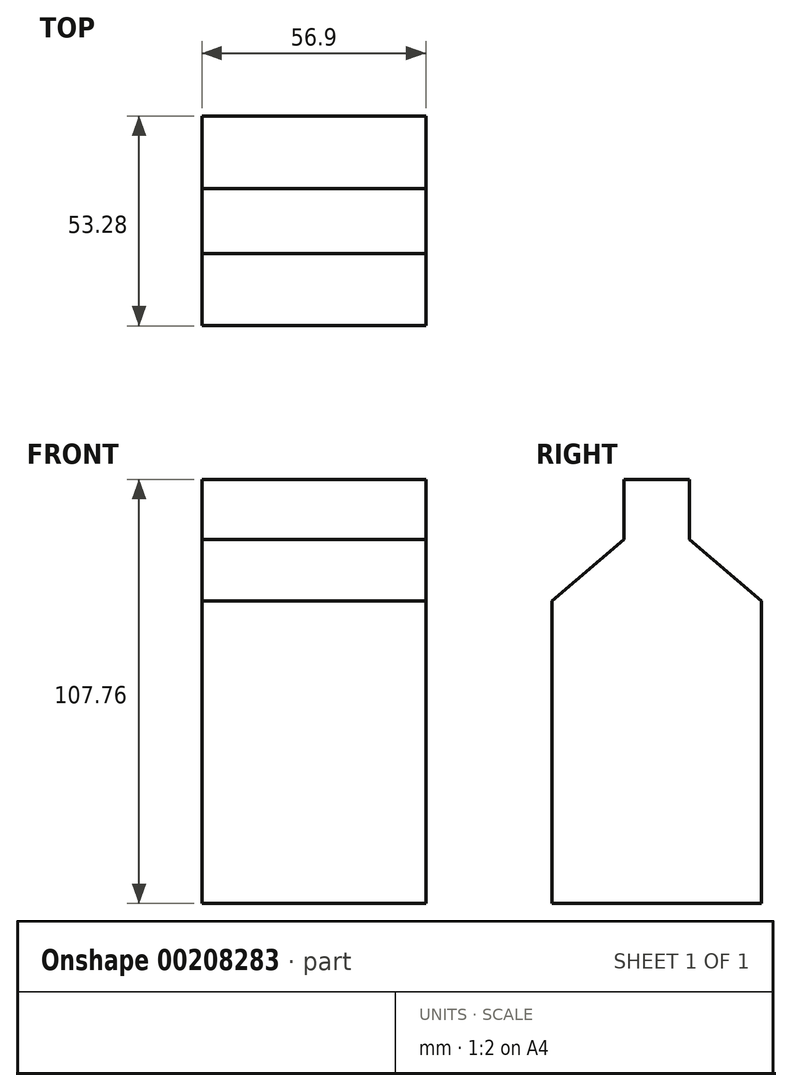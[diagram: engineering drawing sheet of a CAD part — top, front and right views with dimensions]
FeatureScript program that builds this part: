
annotation { "Feature Type Name" : "Feature", "Feature Type Description" : "" }
export const myFeature = defineFeature(function(context is Context, id is Id, definition is map)
    precondition{}
    {
        {
            var Q0;
            Q0=qCreatedBy(makeId("Right.planeOp"),FACE);
            var sketch = newSketch(context, id + "F0", { "sketchPlane" : qUnion([Q0])});
            skLineSegment(sketch, "E0.bottom", {"start": v(26.64, -38.44) * mm, "end": v(-26.64, -38.44) * mm});
            skLineSegment(sketch, "E0.left", {"start": v(26.64, -38.44) * mm, "end": v(26.64, 38.44) * mm});
            skLineSegment(sketch, "E0.right", {"start": v(-26.64, -38.44) * mm, "end": v(-26.64, 38.44) * mm});
            skPoint(sketch, "E0.middle", {"position": v(0, 0) * mm});
            skLineSegment(sketch, "E1", {"start": v(26.64, 38.44) * mm, "end": v(8.27, 53.98) * mm});
            skLineSegment(sketch, "E2", {"start": v(8.27, 53.98) * mm, "end": v(8.27, 69.32) * mm});
            skLineSegment(sketch, "E3", {"start": v(8.27, 69.32) * mm, "end": v(0, 69.32) * mm});
            skLineSegment(sketch, "E4.MirrorCS", {"start": v(-8.27, 69.32) * mm, "end": v(0, 69.32) * mm});
            skLineSegment(sketch, "E5.MirrorCS", {"start": v(-8.27, 53.98) * mm, "end": v(-8.27, 69.32) * mm});
            skLineSegment(sketch, "E6.MirrorCS", {"start": v(-26.64, 38.44) * mm, "end": v(-8.27, 53.98) * mm});
            skSolve(sketch);
        }
        {
            var Q0;
            Q0=makeQuery(id+"F0.imprint","IMPRINT",FACE,{"disambiguationData":[TD([[makeQuery(id+"F0.imprint","IMPRINT",EDGE,{"derivedFrom":sQuery(id+"F0.wireOp",EDGE,"E0.bottom")}),-1.0]])]});
            extrude(context, id + "F1", {"entities" : qUnion([Q0]), "endBound" : BoundingType.SYMMETRIC, "oppositeDirection" : true, "depth" : 56.9 * mm});
        }
    });
